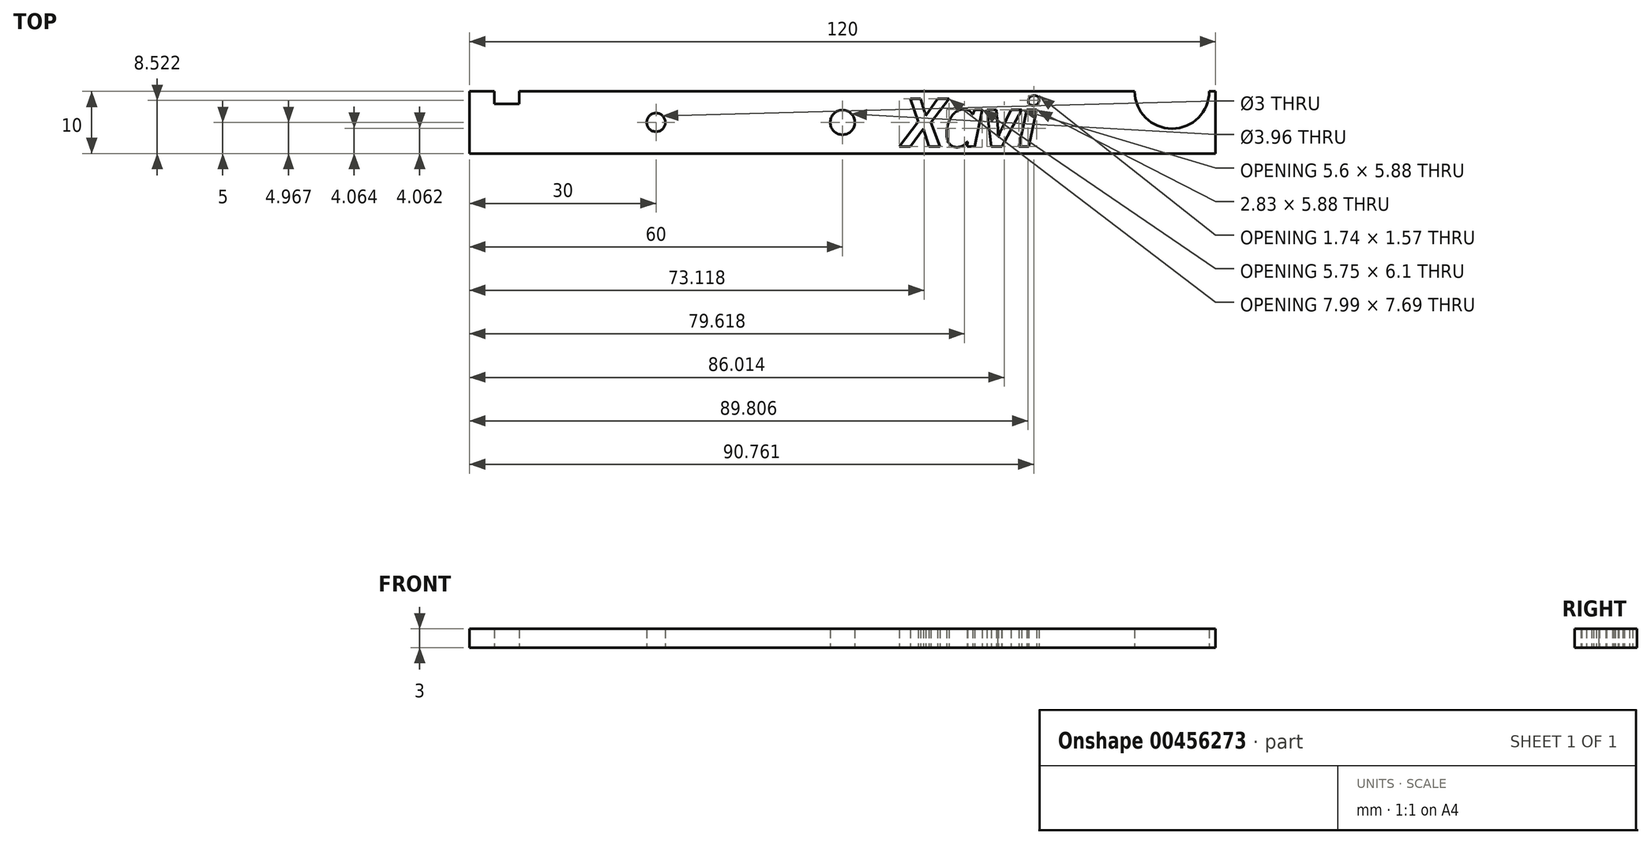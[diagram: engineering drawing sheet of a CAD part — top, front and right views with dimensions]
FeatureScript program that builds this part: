
annotation { "Feature Type Name" : "Feature", "Feature Type Description" : "" }
export const myFeature = defineFeature(function(context is Context, id is Id, definition is map)
    precondition{}
    {
        {
            var Q0;
            Q0=qCreatedBy(makeId("Top.planeOp"),FACE);
            var sketch = newSketch(context, id + "F0", { "sketchPlane" : qUnion([Q0])});
            skLineSegment(sketch, "E0.bottom", {"start": v(60, -5) * mm, "end": v(-60, -5) * mm});
            skLineSegment(sketch, "E0.top", {"start": v(60, 5) * mm, "end": v(-60, 5) * mm});
            skLineSegment(sketch, "E0.left", {"start": v(60, -5) * mm, "end": v(60, 5) * mm});
            skLineSegment(sketch, "E0.right", {"start": v(-60, -5) * mm, "end": v(-60, 5) * mm});
            skPoint(sketch, "E0.middle", {"position": v(0, 0) * mm});
            skCircle(sketch, "E1", {"center": v(0, 0) * mm, "radius": 1.98 * mm});
            skCircle(sketch, "E2", {"center": v(0, 0) * mm, "radius": 8.53 * mm});
            skLineSegment(sketch, "E3.bottom", {"start": v(-56, 5) * mm, "end": v(-52, 5) * mm});
            skLineSegment(sketch, "E3.top", {"start": v(-56, 3) * mm, "end": v(-52, 3) * mm});
            skLineSegment(sketch, "E3.left", {"start": v(-56, 5) * mm, "end": v(-56, 3) * mm});
            skLineSegment(sketch, "E3.right", {"start": v(-52, 5) * mm, "end": v(-52, 3) * mm});
            skCircle(sketch, "E4", {"center": v(-30, 0) * mm, "radius": 1.5 * mm});
            skCircle(sketch, "E5", {"center": v(53, 5) * mm, "radius": 6 * mm});
            skText(sketch, "E6", { "text": "Xavi", "fontName": "NotoSans-BoldItalic.ttf"});
            skLineSegment(sketch, "E7", {"start": v(0, 0) * mm, "end": v(45.6, 0) * mm, "construction": true});
            skLineSegment(sketch, "E8", {"start": v(9.74, 0) * mm, "end": v(15.11, 0) * mm, "construction": true});
            const initialGuessF0  = {"E6": [0.00974, -0.00388, 1, 0, 0.00776]};
            skSetInitialGuess(sketch, initialGuessF0);
            skSolve(sketch);
        }
        {
            var Q0;
            {var subQ0=sQuery(id+"F0.wireOp",EDGE,"E2");var subQ1=sQuery(id+"F0.wireOp",EDGE,"E0.bottom");var subQ2=makeQuery(id+"F0.imprint","INTERSECT",VERTEX,{"disambiguationData":[OD(0.0)],"derivedFrom":[subQ1,subQ0]});Q0=makeQuery(id+"F0.imprint","IMPRINT",FACE,{"disambiguationData":[TD([[makeQuery(id+"F0.imprint","IMPRINT",EDGE,{"disambiguationData":[TD([[subQ2,-1.0]])],"derivedFrom":subQ1}),1.0]])]});}
            var Q1;
            {var subQ0=sQuery(id+"F0.wireOp",EDGE,"E2");var subQ1=sQuery(id+"F0.wireOp",EDGE,"E0.top");var subQ2=makeQuery(id+"F0.imprint","INTERSECT",VERTEX,{"disambiguationData":[OD(0.0)],"derivedFrom":[subQ1,subQ0]});Q1=makeQuery(id+"F0.imprint","IMPRINT",FACE,{"disambiguationData":[TD([[makeQuery(id+"F0.imprint","IMPRINT",EDGE,{"disambiguationData":[TD([[subQ2,-1.0]])],"derivedFrom":subQ1}),-1.0]])]});}
            var Q2;
            {var subQ0=sQuery(id+"F0.wireOp",EDGE,"E0.left");Q2=makeQuery(id+"F0.imprint","IMPRINT",FACE,{"disambiguationData":[TD([[makeQuery(id+"F0.imprint","IMPRINT",EDGE,{"derivedFrom":subQ0}),1.0]])]});}
            var Q3;
            {var subQ0=sQuery(id+"F0.wireOp",EDGE,"E0.right");Q3=makeQuery(id+"F0.imprint","IMPRINT",FACE,{"disambiguationData":[TD([[makeQuery(id+"F0.imprint","IMPRINT",EDGE,{"derivedFrom":subQ0}),-1.0]])]});}
            var Q4;
            Q4=makeQuery(id+"F0.imprint","IMPRINT",FACE,{"disambiguationData":[TD([[makeQuery(id+"F0.imprint","IMPRINT",EDGE,{"derivedFrom":sQuery(id+"F0.wireOp",EDGE,"E1")}),-1.0]])]});
            extrude(context, id + "F1", {"entities" : qUnion([Q0, Q1, Q2, Q3, Q4]), "depth" : 3 * mm});
        }
    });
